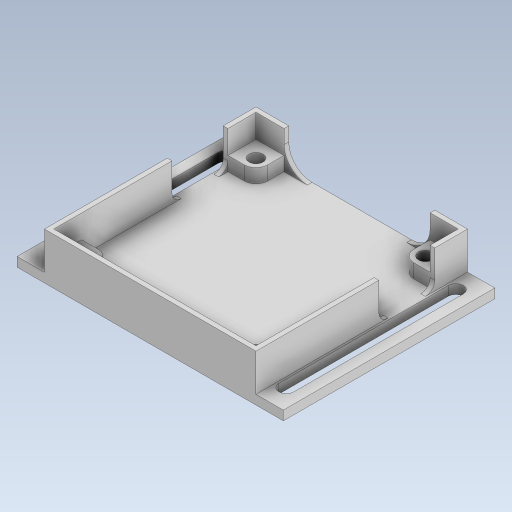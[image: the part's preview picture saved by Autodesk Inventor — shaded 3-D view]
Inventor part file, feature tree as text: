
AUTODESK INVENTOR PART (.ipt)
format: ipt  version: 2023.5 (Build 275446000, 446)  size: 250,368 bytes
history: native  units: mm
features: extrude x7, sketch x4
ambient origin geometry x8: Origin, YZ Plane, XZ Plane, XY Plane, X Axis, Y Axis, Z Axis, Center Point
bodies: Solid1 (feature_tree)
feature tree (11):
  sketch  "Sketch1"  dims[d0=43.3mm d1=43.3mm]
  extrude  "Extrusion1"  Depth=43.3mm
  extrude  "Extrusion2"  Depth=45.3mm
  extrude  "Extrusion3"  Depth=5.0mm
  extrude  "Extrusion4"  Depth=3.0mm
  extrude  "Extrusion5"  Depth=10.0mm TaperAngle=0.0deg
  extrude  "Extrusion6"  Depth=2.0mm TaperAngle=0.0deg
  extrude  "Extrusion7"  Depth=5.0mm TaperAngle=0.0deg
  sketch  "Sketch2"  dims[d2=45.3mm d3=45.3mm]
  sketch  "Sketch3"  dims[d4=5.0mm d5=3.5mm]
  sketch  "Sketch4"  dims[d6=3.5mm d7=3.0mm d8=10.0mm d9=0.0mm d10=2.0mm d11=0.0mm d12=5.0mm d13=0.0mm d14=3.0mm d15=57.0mm d16=3.2mm d17=2.0mm d18=2.0mm d19=0.0mm d20=45.3mm d21=2.0mm d22=0.0mm d23=5.0mm d24=2.0mm d25=2.0mm d26=0.0mm d27=12.0mm d28=2.0mm d29=2.0mm d30=0.0mm]
